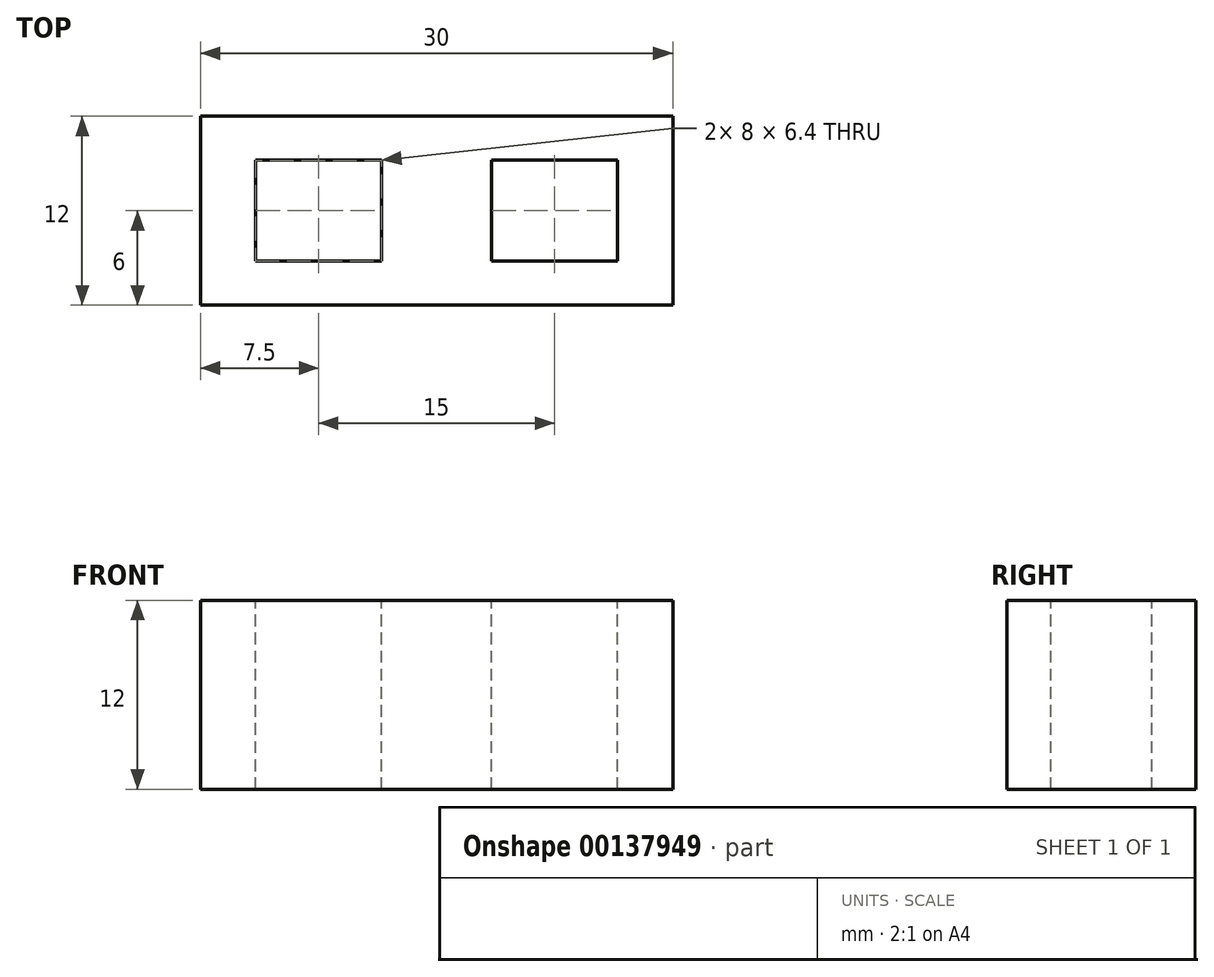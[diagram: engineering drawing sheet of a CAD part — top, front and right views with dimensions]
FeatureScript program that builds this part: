
annotation { "Feature Type Name" : "Feature", "Feature Type Description" : "" }
export const myFeature = defineFeature(function(context is Context, id is Id, definition is map)
    precondition{}
    {
        {
            var Q0;
            Q0=qCreatedBy(makeId("Top.planeOp"),FACE);
            var sketch = newSketch(context, id + "F0", { "sketchPlane" : qUnion([Q0])});
            skLineSegment(sketch, "E0.bottom", {"start": v(0, 0) * mm, "end": v(30, 0) * mm});
            skLineSegment(sketch, "E0.top", {"start": v(0, 12) * mm, "end": v(30, 12) * mm});
            skLineSegment(sketch, "E0.left", {"start": v(0, 0) * mm, "end": v(0, 12) * mm});
            skLineSegment(sketch, "E0.right", {"start": v(30, 0) * mm, "end": v(30, 12) * mm});
            skSolve(sketch);
        }
        {
            var Q0;
            Q0=makeQuery(id+"F0.imprint","IMPRINT",FACE,{"disambiguationData":[TD([[makeQuery(id+"F0.imprint","IMPRINT",EDGE,{"derivedFrom":sQuery(id+"F0.wireOp",EDGE,"E0.bottom")}),1.0]])]});
            extrude(context, id + "F1", {"entities" : qUnion([Q0]), "depth" : 12 * mm});
        }
        {
            var Q0;
            Q0=makeQuery(id+"F1.opExtrude","CAP_FACE",FACE,{"disambiguationData":[OSD([sQuery(id+"F0.wireOp",EDGE,"E0.bottom"),sQuery(id+"F0.wireOp",EDGE,"E0.top"),sQuery(id+"F0.wireOp",EDGE,"E0.left"),sQuery(id+"F0.wireOp",EDGE,"E0.right")])],"isStart":false});
            var sketch = newSketch(context, id + "F2", { "sketchPlane" : qUnion([Q0])});
            skLineSegment(sketch, "E1", {"start": v(0, 6) * mm, "end": v(30, 6) * mm, "construction": true});
            skLineSegment(sketch, "E2", {"start": v(15, 12) * mm, "end": v(15, 0) * mm, "construction": true});
            skLineSegment(sketch, "E3", {"start": v(15, 12) * mm, "end": v(30, 0) * mm, "construction": true});
            skLineSegment(sketch, "E4", {"start": v(0, 12) * mm, "end": v(15, 0) * mm, "construction": true});
            skLineSegment(sketch, "E5", {"start": v(30, 12) * mm, "end": v(15, 0) * mm, "construction": true});
            skLineSegment(sketch, "E6", {"start": v(0, 0) * mm, "end": v(15, 12) * mm, "construction": true});
            skLineSegment(sketch, "E7.bottom", {"start": v(11.5, 9.2) * mm, "end": v(3.5, 9.2) * mm});
            skLineSegment(sketch, "E7.top", {"start": v(11.5, 2.8) * mm, "end": v(3.5, 2.8) * mm});
            skLineSegment(sketch, "E7.left", {"start": v(11.5, 9.2) * mm, "end": v(11.5, 2.8) * mm});
            skLineSegment(sketch, "E7.right", {"start": v(3.5, 9.2) * mm, "end": v(3.5, 2.8) * mm});
            skPoint(sketch, "E7.middle", {"position": v(7.5, 6) * mm});
            skLineSegment(sketch, "E8.MirrorCS", {"start": v(26.5, 9.2) * mm, "end": v(26.5, 2.8) * mm});
            skLineSegment(sketch, "E9.MirrorCS", {"start": v(18.5, 9.2) * mm, "end": v(26.5, 9.2) * mm});
            skLineSegment(sketch, "E10.MirrorCS", {"start": v(18.5, 9.2) * mm, "end": v(18.5, 2.8) * mm});
            skLineSegment(sketch, "E11.MirrorCS", {"start": v(18.5, 2.8) * mm, "end": v(26.5, 2.8) * mm});
            skSolve(sketch);
        }
        {
            var Q0;
            Q0=makeQuery(id+"F2.imprint","IMPRINT",FACE,{"disambiguationData":[TD([[makeQuery(id+"F2.imprint","IMPRINT",EDGE,{"derivedFrom":sQuery(id+"F2.wireOp",EDGE,"E7.bottom")}),1.0]])]});
            var Q1;
            Q1=makeQuery(id+"F2.imprint","IMPRINT",FACE,{"disambiguationData":[TD([[makeQuery(id+"F2.imprint","IMPRINT",EDGE,{"derivedFrom":sQuery(id+"F2.wireOp",EDGE,"E8.MirrorCS")}),-1.0]])]});
            extrude(context, id + "F3", {"entities" : qUnion([Q0, Q1]), "operationType" : NewBodyOperationType.REMOVE, "endBound" : BoundingType.THROUGH_ALL, "oppositeDirection" : true, "depth" : 25 * mm});
        }
    });
